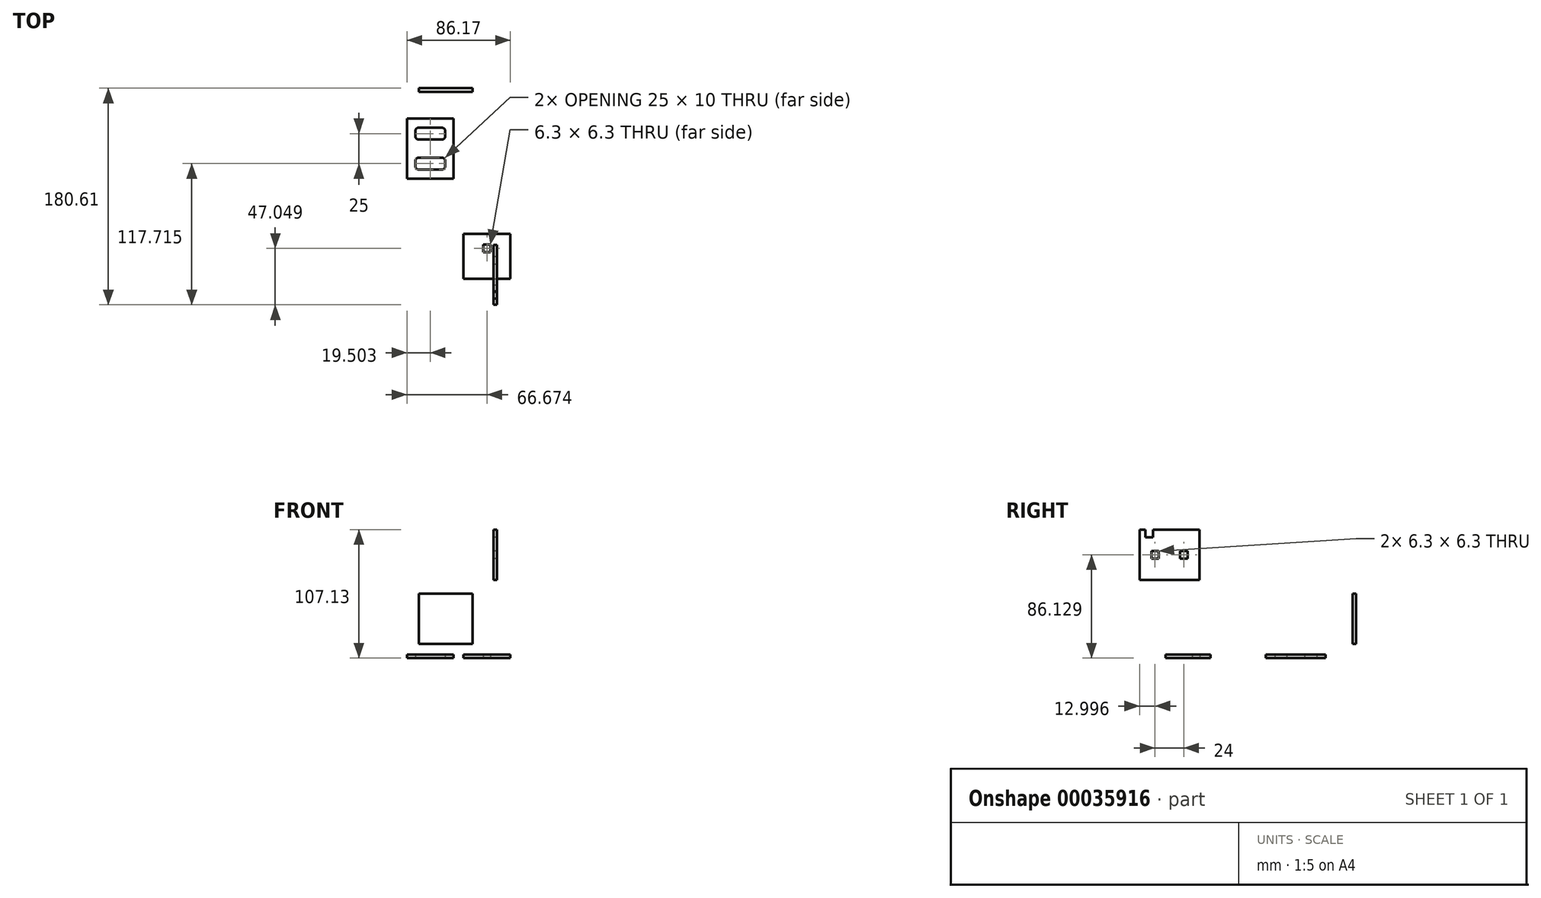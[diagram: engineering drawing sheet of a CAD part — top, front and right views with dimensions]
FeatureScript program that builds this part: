
annotation { "Feature Type Name" : "Feature", "Feature Type Description" : "" }
export const myFeature = defineFeature(function(context is Context, id is Id, definition is map)
    precondition{}
    {
        {
            var Q0;
            Q0=qCreatedBy(makeId("Top.planeOp"),FACE);
            var sketch = newSketch(context, id + "F0", { "sketchPlane" : qUnion([Q0])});
            skLineSegment(sketch, "E0.bottom", {"start": v(-25.06, -158.86) * mm, "end": v(13.94, -158.86) * mm});
            skLineSegment(sketch, "E0.top", {"start": v(-25.06, -121.56) * mm, "end": v(13.94, -121.56) * mm});
            skLineSegment(sketch, "E0.left", {"start": v(-25.06, -158.86) * mm, "end": v(-25.06, -121.56) * mm});
            skLineSegment(sketch, "E0.right", {"start": v(13.94, -158.86) * mm, "end": v(13.94, -121.56) * mm});
            skPoint(sketch, "E1.rect.middle.positionSnap0", {"position": v(-5.56, -158.86) * mm});
            skPoint(sketch, "E1.rect.centerSnap0", {"position": v(-5.56, -158.86) * mm});
            skLineSegment(sketch, "E2.rect.bottom", {"start": v(-8.7, -130.41) * mm, "end": v(-2.4, -130.41) * mm});
            skLineSegment(sketch, "E2.rect.top", {"start": v(-8.7, -136.71) * mm, "end": v(-2.4, -136.71) * mm});
            skLineSegment(sketch, "E2.rect.left", {"start": v(-8.7, -130.41) * mm, "end": v(-8.7, -136.71) * mm});
            skLineSegment(sketch, "E2.rect.right", {"start": v(-2.4, -130.41) * mm, "end": v(-2.4, -136.71) * mm});
            skPoint(sketch, "E2.rect.middle", {"position": v(-5.56, -133.56) * mm});
            skPoint(sketch, "E2.rect.middle.positionSnap0", {"position": v(-5.56, -121.56) * mm});
            skPoint(sketch, "E2.rect.centerSnap0", {"position": v(-5.56, -121.56) * mm});
            skSolve(sketch);
        }
        {
            var Q0;
            Q0 = qSketchRegion(id + "F0", true);
            extrude(context, id + "F1", {"entities" : qUnion([Q0]), "depth" : 3 * mm});
        }
        {
            var Q0;
            Q0=qCreatedBy(makeId("Right.planeOp"),FACE);
            var sketch = newSketch(context, id + "F2", { "sketchPlane" : qUnion([Q0])});
            skLineSegment(sketch, "E3.rect.bottom", {"start": v(-130.61, 65.13) * mm, "end": v(-180.61, 65.13) * mm});
            skLineSegment(sketch, "E3.rect.left", {"start": v(-130.61, 65.13) * mm, "end": v(-130.61, 107.13) * mm});
            skLineSegment(sketch, "E3.rect.right", {"start": v(-180.61, 65.13) * mm, "end": v(-180.61, 107.13) * mm});
            skPoint(sketch, "E3.rect.middle", {"position": v(-155.61, 86.13) * mm});
            skLineSegment(sketch, "E4.rect.bottom", {"start": v(-140.46, 89.28) * mm, "end": v(-146.76, 89.28) * mm});
            skLineSegment(sketch, "E4.rect.top", {"start": v(-140.46, 82.98) * mm, "end": v(-146.76, 82.98) * mm});
            skLineSegment(sketch, "E4.rect.left", {"start": v(-140.46, 89.28) * mm, "end": v(-140.46, 82.98) * mm});
            skLineSegment(sketch, "E4.rect.right", {"start": v(-146.76, 89.28) * mm, "end": v(-146.76, 82.98) * mm});
            skPoint(sketch, "E4.rect.middle", {"position": v(-143.61, 86.13) * mm});
            skPoint(sketch, "E4.rect.middle.positionSnap0", {"position": v(-130.61, 86.13) * mm});
            skPoint(sketch, "E4.rect.centerSnap0", {"position": v(-130.61, 86.13) * mm});
            skLineSegment(sketch, "E5.rect.bottom", {"start": v(-169.31, 100.83) * mm, "end": v(-175.61, 100.83) * mm});
            skLineSegment(sketch, "E5.rect.left", {"start": v(-169.31, 100.83) * mm, "end": v(-169.31, 107.13) * mm});
            skLineSegment(sketch, "E5.rect.right", {"start": v(-175.61, 100.83) * mm, "end": v(-175.61, 107.13) * mm});
            skPoint(sketch, "E5.rect.middle", {"position": v(-172.46, 103.98) * mm});
            skLineSegment(sketch, "E6", {"start": v(-175.61, 107.13) * mm, "end": v(-180.61, 107.13) * mm});
            skLineSegment(sketch, "E7", {"start": v(-169.31, 107.13) * mm, "end": v(-130.61, 107.13) * mm});
            skLineSegment(sketch, "E8.rect.bottom", {"start": v(-164.46, 82.98) * mm, "end": v(-170.76, 82.98) * mm});
            skLineSegment(sketch, "E8.rect.top", {"start": v(-164.46, 89.28) * mm, "end": v(-170.76, 89.28) * mm});
            skLineSegment(sketch, "E8.rect.left", {"start": v(-164.46, 82.98) * mm, "end": v(-164.46, 89.28) * mm});
            skLineSegment(sketch, "E8.rect.right", {"start": v(-170.76, 82.98) * mm, "end": v(-170.76, 89.28) * mm});
            skPoint(sketch, "E8.rect.middle", {"position": v(-167.61, 86.13) * mm});
            skSolve(sketch);
        }
        {
            var Q0;
            Q0 = qSketchRegion(id + "F2", true);
            extrude(context, id + "F3", {"entities" : qUnion([Q0]), "depth" : 3 * mm});
        }
        {
            var Q0;
            Q0=qCreatedBy(makeId("Top.planeOp"),FACE);
            var sketch = newSketch(context, id + "F4", { "sketchPlane" : qUnion([Q0])});
            skLineSegment(sketch, "E9.rect.bottom", {"start": v(-33.23, -25.4) * mm, "end": v(-72.23, -25.4) * mm});
            skLineSegment(sketch, "E9.rect.top", {"start": v(-33.23, -75.4) * mm, "end": v(-72.23, -75.4) * mm});
            skLineSegment(sketch, "E9.rect.left", {"start": v(-33.23, -25.4) * mm, "end": v(-33.23, -75.4) * mm});
            skLineSegment(sketch, "E9.rect.right", {"start": v(-72.23, -25.4) * mm, "end": v(-72.23, -75.4) * mm});
            skPoint(sketch, "E9.rect.middle", {"position": v(-52.73, -50.4) * mm});
            skLineSegment(sketch, "E10.rect.bottom", {"start": v(-62.23, -57.9) * mm, "end": v(-43.23, -57.9) * mm});
            skLineSegment(sketch, "E10.rect.top", {"start": v(-62.23, -67.9) * mm, "end": v(-43.23, -67.9) * mm});
            skLineSegment(sketch, "E10.rect.left", {"start": v(-65.23, -60.9) * mm, "end": v(-65.23, -64.9) * mm});
            skLineSegment(sketch, "E10.rect.right", {"start": v(-40.23, -60.9) * mm, "end": v(-40.23, -64.9) * mm});
            skPoint(sketch, "E10.rect.middle", {"position": v(-52.73, -62.9) * mm});
            skLineSegment(sketch, "E11.rect.bottom", {"start": v(-62.23, -42.9) * mm, "end": v(-43.23, -42.9) * mm});
            skLineSegment(sketch, "E11.rect.top", {"start": v(-62.23, -32.9) * mm, "end": v(-43.23, -32.9) * mm});
            skLineSegment(sketch, "E11.rect.left", {"start": v(-65.23, -39.9) * mm, "end": v(-65.23, -35.9) * mm});
            skLineSegment(sketch, "E11.rect.right", {"start": v(-40.23, -39.9) * mm, "end": v(-40.23, -35.9) * mm});
            skPoint(sketch, "E11.rect.middle", {"position": v(-52.73, -37.9) * mm});
            skPoint(sketch, "E12.visualSharp", {"position": v(-65.23, -67.9) * mm});
            skArc(sketch, "E12.filletArc", {"start": v(-65.23, -64.9) * mm, "mid": v(-64.35, -67.02) * mm, "end": v(-62.23, -67.9) * mm});
            skPoint(sketch, "E13.visualSharp", {"position": v(-65.23, -57.9) * mm});
            skArc(sketch, "E13.filletArc", {"start": v(-62.23, -57.9) * mm, "mid": v(-64.35, -58.77) * mm, "end": v(-65.23, -60.9) * mm});
            skPoint(sketch, "E14.visualSharp", {"position": v(-65.23, -42.9) * mm});
            skArc(sketch, "E14.filletArc", {"start": v(-65.23, -39.9) * mm, "mid": v(-64.35, -42.02) * mm, "end": v(-62.23, -42.9) * mm});
            skPoint(sketch, "E15.visualSharp", {"position": v(-65.23, -32.9) * mm});
            skArc(sketch, "E15.filletArc", {"start": v(-62.23, -32.9) * mm, "mid": v(-64.35, -33.77) * mm, "end": v(-65.23, -35.9) * mm});
            skPoint(sketch, "E16.visualSharp", {"position": v(-40.23, -32.9) * mm});
            skArc(sketch, "E16.filletArc", {"start": v(-40.23, -35.9) * mm, "mid": v(-41.1, -33.77) * mm, "end": v(-43.23, -32.9) * mm});
            skPoint(sketch, "E17.visualSharp", {"position": v(-40.23, -42.9) * mm});
            skArc(sketch, "E17.filletArc", {"start": v(-43.23, -42.9) * mm, "mid": v(-41.1, -42.02) * mm, "end": v(-40.23, -39.9) * mm});
            skPoint(sketch, "E18.visualSharp", {"position": v(-40.23, -57.9) * mm});
            skArc(sketch, "E18.filletArc", {"start": v(-40.23, -60.9) * mm, "mid": v(-41.1, -58.77) * mm, "end": v(-43.23, -57.9) * mm});
            skPoint(sketch, "E19.visualSharp", {"position": v(-40.23, -67.9) * mm});
            skArc(sketch, "E19.filletArc", {"start": v(-43.23, -67.9) * mm, "mid": v(-41.1, -67.02) * mm, "end": v(-40.23, -64.9) * mm});
            skSolve(sketch);
        }
        {
            var Q0;
            Q0 = qSketchRegion(id + "F4", true);
            extrude(context, id + "F5", {"entities" : qUnion([Q0]), "depth" : 3 * mm});
        }
        {
            var Q0;
            Q0=qCreatedBy(makeId("Front.planeOp"),FACE);
            var sketch = newSketch(context, id + "F6", { "sketchPlane" : qUnion([Q0])});
            skLineSegment(sketch, "E20.bottom", {"start": v(-62.35, 53.86) * mm, "end": v(-17.35, 53.86) * mm});
            skLineSegment(sketch, "E20.top", {"start": v(-62.35, 11.86) * mm, "end": v(-17.35, 11.86) * mm});
            skLineSegment(sketch, "E20.left", {"start": v(-62.35, 53.86) * mm, "end": v(-62.35, 11.86) * mm});
            skLineSegment(sketch, "E20.right", {"start": v(-17.35, 53.86) * mm, "end": v(-17.35, 11.86) * mm});
            skSolve(sketch);
        }
        {
            var Q0;
            Q0 = qSketchRegion(id + "F6", true);
            extrude(context, id + "F7", {"entities" : qUnion([Q0]), "depth" : 3 * mm});
        }
    });
